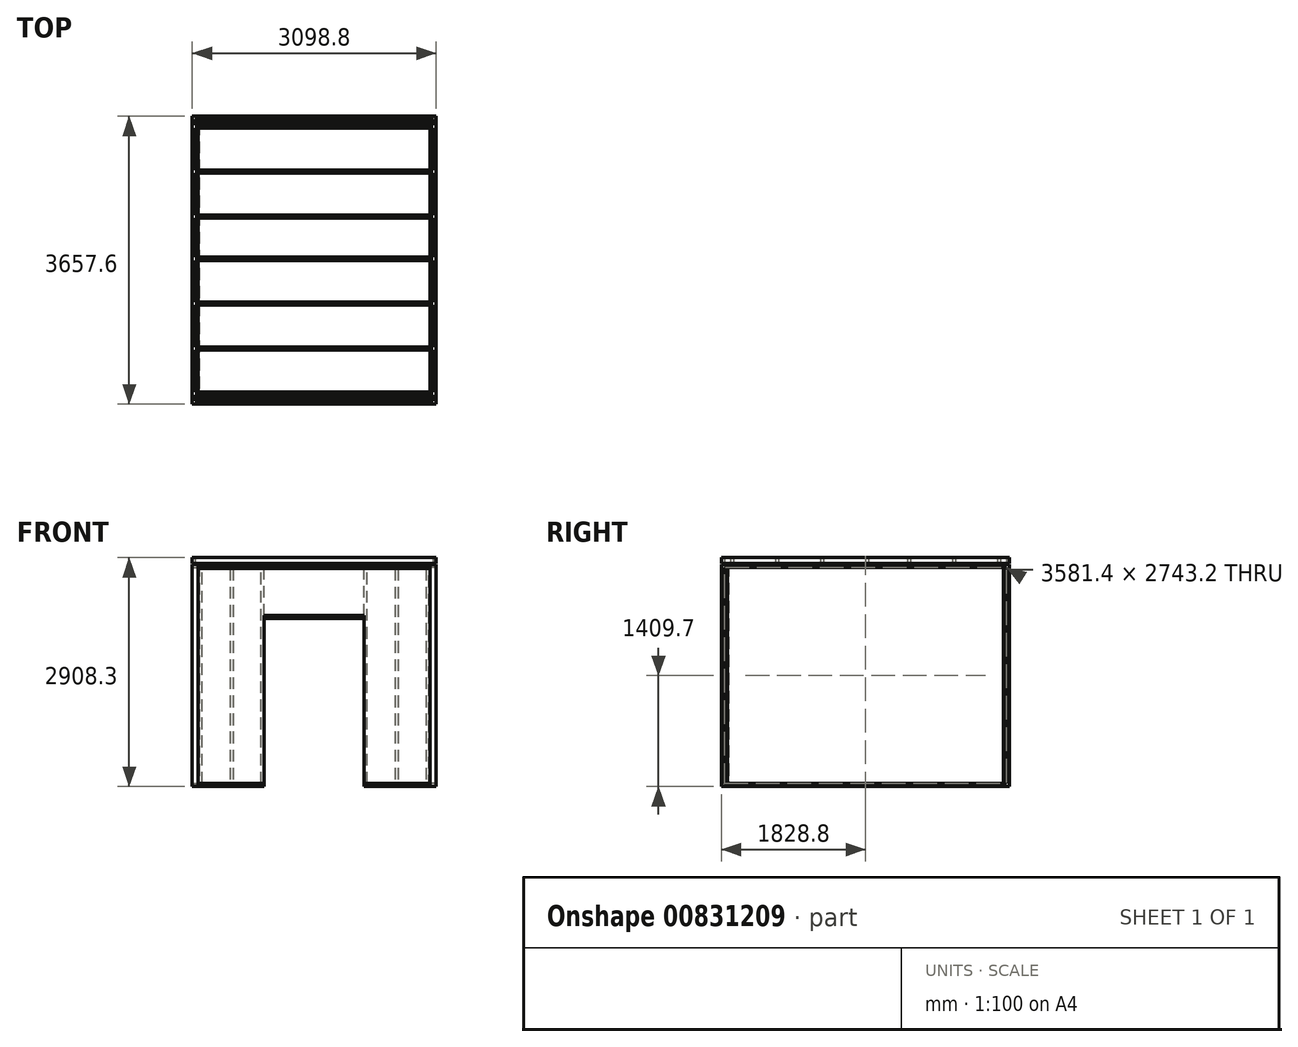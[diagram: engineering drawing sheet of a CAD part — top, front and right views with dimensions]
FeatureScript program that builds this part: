
annotation { "Feature Type Name" : "Feature", "Feature Type Description" : "" }
export const myFeature = defineFeature(function(context is Context, id is Id, definition is map)
    precondition{}
    {
        {
            var Q0;
            Q0=qCreatedBy(makeId("Top.planeOp"),FACE);
            var sketch = newSketch(context, id + "F0", { "sketchPlane" : qUnion([Q0])});
            skLineSegment(sketch, "E0.bottom", {"start": v(-980.79, 2857.66) * mm, "end": v(155.93, 2857.66) * mm});
            skLineSegment(sketch, "E0.top", {"start": v(-980.79, -622.14) * mm, "end": v(1105.1, -622.14) * mm});
            skLineSegment(sketch, "E0.left", {"start": v(-980.79, 2857.66) * mm, "end": v(-980.79, -622.14) * mm});
            skLineSegment(sketch, "E0.right", {"start": v(1940.21, 2857.66) * mm, "end": v(1940.21, -622.14) * mm});
            skLineSegment(sketch, "E1.bottom", {"start": v(-993.49, 2870.36) * mm, "end": v(155.93, 2870.36) * mm});
            skLineSegment(sketch, "E1.top", {"start": v(-993.49, -634.84) * mm, "end": v(913.5, -634.84) * mm});
            skLineSegment(sketch, "E1.left", {"start": v(-993.49, 2870.36) * mm, "end": v(-993.49, -634.84) * mm});
            skLineSegment(sketch, "E1.right", {"start": v(1952.91, 2870.36) * mm, "end": v(1952.91, -634.84) * mm});
            skLineSegment(sketch, "E2.trimOffspring", {"start": v(153.53, 2870.36) * mm, "end": v(1952.91, 2870.36) * mm});
            skLineSegment(sketch, "E3.trimOffspring", {"start": v(149.76, 2857.66) * mm, "end": v(1940.21, 2857.66) * mm});
            skLineSegment(sketch, "E4.trimOffspring", {"start": v(1102.01, -622.14) * mm, "end": v(1940.21, -622.14) * mm});
            skLineSegment(sketch, "E5.trimOffspring", {"start": v(882.21, -634.84) * mm, "end": v(1952.91, -634.84) * mm});
            skSolve(sketch);
        }
        {
            var Q0;
            Q0=makeQuery(id+"F0.imprint","IMPRINT",FACE,{"disambiguationData":[TD([[makeQuery(id+"F0.imprint","IMPRINT",EDGE,{"derivedFrom":sQuery(id+"F0.wireOp",EDGE,"E0.bottom")}),1.0]])]});
            var Q1;
            Q1=makeQuery(id+"F0.imprint","IMPRINT",FACE,{"disambiguationData":[TD([[makeQuery(id+"F0.imprint","IMPRINT",EDGE,{"derivedFrom":sQuery(id+"F0.wireOp",EDGE,"E0.right")}),1.0]])]});
            extrude(context, id + "F1", {"entities" : qUnion([Q0, Q1]), "depth" : 2133.6 * mm + 685.8 * mm, "offsetDistance" : 25.4 * mm});
        }
        {
            var Q0;
            Q0=makeQuery(id+"F1.opExtrude","CAP_FACE",FACE,{"disambiguationData":[OSD([sQuery(id+"F0.wireOp",EDGE,"E0.bottom"),sQuery(id+"F0.wireOp",EDGE,"E0.top"),sQuery(id+"F0.wireOp",EDGE,"E0.left"),sQuery(id+"F0.wireOp",EDGE,"E1.bottom"),sQuery(id+"F0.wireOp",EDGE,"E1.top"),sQuery(id+"F0.wireOp",EDGE,"E1.left"),sQuery(id+"F0.wireOp",EDGE,"ajJvUeQd-ddKz-yDWU-SHTq-AfXzZqwUQA1N.left"),sQuery(id+"F0.wireOp",EDGE,"rDKjrFLu-EuC5-olRp-ZrVZ-GupeaafQM4Xr")])],"isStart":false});
            var sketch = newSketch(context, id + "F2", { "sketchPlane" : qUnion([Q0])});
            skPoint(sketch, "E6.0", {"position": v(1952.91, 2870.36) * mm});
            skPoint(sketch, "E7.0", {"position": v(-993.49, 2870.36) * mm});
            skPoint(sketch, "E8.0", {"position": v(-993.49, -634.84) * mm});
            skLineSegment(sketch, "E9.bottom", {"start": v(-993.49, -634.84) * mm, "end": v(1952.91, -634.84) * mm});
            skLineSegment(sketch, "E9.top", {"start": v(-993.49, 2870.36) * mm, "end": v(1952.91, 2870.36) * mm});
            skLineSegment(sketch, "E9.left", {"start": v(-993.49, -634.84) * mm, "end": v(-993.49, 2870.36) * mm});
            skLineSegment(sketch, "E9.right", {"start": v(1952.91, -634.84) * mm, "end": v(1952.91, 2870.36) * mm});
            skSolve(sketch);
        }
        {
            var Q0;
            Q0 = qSketchRegion(id + "F2", true);
            extrude(context, id + "F3", {"entities" : qUnion([Q0]), "depth" : 12.7 * mm, "offsetDistance" : 25.4 * mm});
        }
        {
            var Q0;
            Q0=makeQuery(id+"F1.opExtrude","SWEPT_FACE",FACE,{"disambiguationData":[OSD([sQuery(id+"F0.wireOp",EDGE,"E1.top"),sQuery(id+"F0.wireOp",EDGE,"E5.trimOffspring")])]});
            var sketch = newSketch(context, id + "F4", { "sketchPlane" : qUnion([Q0])});
            skLineSegment(sketch, "E10.bottom", {"start": v(-155.29, 0) * mm, "end": v(1114.71, 0) * mm});
            skLineSegment(sketch, "E10.top", {"start": v(-155.29, 2133.6) * mm, "end": v(1114.71, 2133.6) * mm});
            skLineSegment(sketch, "E10.left", {"start": v(-155.29, 0) * mm, "end": v(-155.29, 2133.6) * mm});
            skLineSegment(sketch, "E10.right", {"start": v(1114.71, 0) * mm, "end": v(1114.71, 2133.6) * mm});
            skSolve(sketch);
        }
        {
            var Q0;
            Q0=makeQuery(id+"F4.imprint","IMPRINT",FACE,{"disambiguationData":[TD([[makeQuery(id+"F4.imprint","IMPRINT",EDGE,{"derivedFrom":sQuery(id+"F4.wireOp",EDGE,"E10.bottom")}),1.0]])]});
            extrude(context, id + "F5", {"entities" : qUnion([Q0]), "operationType" : NewBodyOperationType.REMOVE, "endBound" : BoundingType.THROUGH_ALL, "oppositeDirection" : true, "depth" : 25.4 * mm, "offsetDistance" : 25.4 * mm});
        }
        {
            var Q0;
            Q0=makeQuery(id+"F1.opExtrude","SWEPT_FACE",FACE,{"disambiguationData":[OSD([sQuery(id+"F0.wireOp",EDGE,"E1.top"),sQuery(id+"F0.wireOp",EDGE,"E5.trimOffspring")])]});
            var sketch = newSketch(context, id + "F6", { "sketchPlane" : qUnion([Q0])});
            skLineSegment(sketch, "E11.bottom", {"start": v(-980.79, 0) * mm, "end": v(-155.29, 0) * mm});
            skLineSegment(sketch, "E11.top", {"start": v(-980.79, 38.1) * mm, "end": v(-155.29, 38.1) * mm});
            skLineSegment(sketch, "E11.right", {"start": v(-155.29, 0) * mm, "end": v(-155.29, 38.1) * mm});
            skLineSegment(sketch, "E12.bottom", {"start": v(-980.79, 38.1) * mm, "end": v(-942.69, 38.1) * mm});
            skLineSegment(sketch, "E12.top", {"start": v(-980.79, 2768.6) * mm, "end": v(-942.69, 2768.6) * mm});
            skLineSegment(sketch, "E12.left", {"start": v(-980.79, 38.1) * mm, "end": v(-980.79, 2768.6) * mm});
            skLineSegment(sketch, "E12.right", {"start": v(-942.69, 38.1) * mm, "end": v(-942.69, 2768.6) * mm});
            skLineSegment(sketch, "E13.bottom", {"start": v(-980.79, 2768.6) * mm, "end": v(1940.21, 2768.6) * mm});
            skLineSegment(sketch, "E13.top", {"start": v(-980.79, 2806.7) * mm, "end": v(1940.21, 2806.7) * mm});
            skLineSegment(sketch, "E13.left", {"start": v(-980.79, 2768.6) * mm, "end": v(-980.79, 2806.7) * mm});
            skLineSegment(sketch, "E13.right", {"start": v(1940.21, 2768.6) * mm, "end": v(1940.21, 2806.7) * mm});
            skLineSegment(sketch, "E14.bottom", {"start": v(1940.21, 2768.6) * mm, "end": v(1902.11, 2768.6) * mm});
            skLineSegment(sketch, "E14.top", {"start": v(1940.21, 38.1) * mm, "end": v(1902.11, 38.1) * mm});
            skLineSegment(sketch, "E14.left", {"start": v(1940.21, 2768.6) * mm, "end": v(1940.21, 38.1) * mm});
            skLineSegment(sketch, "E14.right", {"start": v(1902.11, 2768.6) * mm, "end": v(1902.11, 38.1) * mm});
            skLineSegment(sketch, "E15.bottom", {"start": v(1940.21, 38.1) * mm, "end": v(1114.71, 38.1) * mm});
            skLineSegment(sketch, "E15.top", {"start": v(1940.21, 0) * mm, "end": v(1114.71, 0) * mm});
            skLineSegment(sketch, "E15.left", {"start": v(1940.21, 38.1) * mm, "end": v(1940.21, 0) * mm});
            skLineSegment(sketch, "E15.right", {"start": v(1114.71, 38.1) * mm, "end": v(1114.71, 0) * mm});
            skLineSegment(sketch, "E16.bottom", {"start": v(1114.71, 38.1) * mm, "end": v(1152.81, 38.1) * mm});
            skLineSegment(sketch, "E16.top", {"start": v(1114.71, 2768.6) * mm, "end": v(1152.81, 2768.6) * mm});
            skLineSegment(sketch, "E16.left", {"start": v(1114.71, 38.1) * mm, "end": v(1114.71, 2768.6) * mm});
            skLineSegment(sketch, "E16.right", {"start": v(1152.81, 38.1) * mm, "end": v(1152.81, 2768.6) * mm});
            skLineSegment(sketch, "E17.bottom", {"start": v(1114.71, 2133.6) * mm, "end": v(-155.29, 2133.6) * mm});
            skLineSegment(sketch, "E17.top", {"start": v(1114.71, 2171.7) * mm, "end": v(-155.29, 2171.7) * mm});
            skLineSegment(sketch, "E17.left", {"start": v(1114.71, 2133.6) * mm, "end": v(1114.71, 2171.7) * mm});
            skLineSegment(sketch, "E17.right", {"start": v(-155.29, 2133.6) * mm, "end": v(-155.29, 2171.7) * mm});
            skLineSegment(sketch, "E18.bottom", {"start": v(-155.29, 38.1) * mm, "end": v(-193.39, 38.1) * mm});
            skLineSegment(sketch, "E18.top", {"start": v(-155.29, 2768.6) * mm, "end": v(-193.39, 2768.6) * mm});
            skLineSegment(sketch, "E18.left", {"start": v(-155.29, 38.1) * mm, "end": v(-155.29, 2768.6) * mm});
            skLineSegment(sketch, "E18.right", {"start": v(-193.39, 38.1) * mm, "end": v(-193.39, 2768.6) * mm});
            skLineSegment(sketch, "E19.bottom", {"start": v(-587.09, 2768.6) * mm, "end": v(-548.99, 2768.6) * mm});
            skLineSegment(sketch, "E19.top", {"start": v(-587.09, 38.1) * mm, "end": v(-548.99, 38.1) * mm});
            skLineSegment(sketch, "E19.left", {"start": v(-587.09, 2768.6) * mm, "end": v(-587.09, 38.1) * mm});
            skLineSegment(sketch, "E19.right", {"start": v(-548.99, 2768.6) * mm, "end": v(-548.99, 38.1) * mm});
            skLineSegment(sketch, "E20.bottom", {"start": v(1508.41, 2768.6) * mm, "end": v(1546.51, 2768.6) * mm});
            skLineSegment(sketch, "E20.top", {"start": v(1508.41, 38.1) * mm, "end": v(1546.51, 38.1) * mm});
            skLineSegment(sketch, "E20.left", {"start": v(1508.41, 2768.6) * mm, "end": v(1508.41, 38.1) * mm});
            skLineSegment(sketch, "E20.right", {"start": v(1546.51, 2768.6) * mm, "end": v(1546.51, 38.1) * mm});
            skLineSegment(sketch, "E21", {"start": v(-980.79, 38.1) * mm, "end": v(-980.79, 0) * mm});
            skSolve(sketch);
        }
        {
            var Q0;
            Q0=makeQuery(id+"F6.imprint","IMPRINT",FACE,{"disambiguationData":[TD([[makeQuery(id+"F6.imprint","IMPRINT",EDGE,{"derivedFrom":sQuery(id+"F6.wireOp",EDGE,"E13.top")}),-1.0]])]});
            var Q1;
            Q1=makeQuery(id+"F6.imprint","IMPRINT",FACE,{"disambiguationData":[TD([[makeQuery(id+"F6.imprint","IMPRINT",EDGE,{"derivedFrom":sQuery(id+"F6.wireOp",EDGE,"E12.bottom")}),1.0]])]});
            var Q2;
            Q2=makeQuery(id+"F6.imprint","IMPRINT",FACE,{"disambiguationData":[TD([[makeQuery(id+"F6.imprint","IMPRINT",EDGE,{"derivedFrom":sQuery(id+"F6.wireOp",EDGE,"E19.bottom")}),-1.0]])]});
            var Q3;
            {var subQ3=sQuery(id+"F6.wireOp",EDGE,"E18.bottom");Q3=makeQuery(id+"F6.imprint","IMPRINT",FACE,{"disambiguationData":[TD([[makeQuery(id+"F6.imprint","IMPRINT",EDGE,{"derivedFrom":subQ3}),-1.0]])]});}
            var Q4;
            {var subQ0=sQuery(id+"F6.wireOp",EDGE,"E17.bottom");Q4=makeQuery(id+"F6.imprint","IMPRINT",FACE,{"disambiguationData":[TD([[makeQuery(id+"F6.imprint","IMPRINT",EDGE,{"derivedFrom":subQ0}),1.0]])]});}
            var Q5;
            {var subQ3=sQuery(id+"F6.wireOp",EDGE,"E16.bottom");Q5=makeQuery(id+"F6.imprint","IMPRINT",FACE,{"disambiguationData":[TD([[makeQuery(id+"F6.imprint","IMPRINT",EDGE,{"derivedFrom":subQ3}),1.0]])]});}
            var Q6;
            Q6=makeQuery(id+"F6.imprint","IMPRINT",FACE,{"disambiguationData":[TD([[makeQuery(id+"F6.imprint","IMPRINT",EDGE,{"derivedFrom":sQuery(id+"F6.wireOp",EDGE,"E20.bottom")}),-1.0]])]});
            var Q7;
            Q7=makeQuery(id+"F6.imprint","IMPRINT",FACE,{"disambiguationData":[TD([[makeQuery(id+"F6.imprint","IMPRINT",EDGE,{"derivedFrom":sQuery(id+"F6.wireOp",EDGE,"E14.bottom")}),1.0]])]});
            var Q8;
            Q8=makeQuery(id+"F6.imprint","IMPRINT",FACE,{"disambiguationData":[TD([[makeQuery(id+"F6.imprint","IMPRINT",EDGE,{"derivedFrom":sQuery(id+"F6.wireOp",EDGE,"E15.top")}),1.0]])]});
            var Q9;
            Q9=makeQuery(id+"F6.imprint","IMPRINT",FACE,{"disambiguationData":[TD([[makeQuery(id+"F6.imprint","IMPRINT",EDGE,{"derivedFrom":sQuery(id+"F6.wireOp",EDGE,"E11.bottom")}),1.0]])]});
            extrude(context, id + "F7", {"entities" : qUnion([Q0, Q1, Q2, Q3, Q4, Q5, Q6, Q7, Q8, Q9]), "operationType" : NewBodyOperationType.ADD, "depth" : 76.2 * mm, "offsetDistance" : 25.4 * mm});
        }
        {
            var Q0;
            Q0=makeQuery(id+"F1.opExtrude","SWEPT_FACE",FACE,{"disambiguationData":[OSD([sQuery(id+"F0.wireOp",EDGE,"E1.bottom"),sQuery(id+"F0.wireOp",EDGE,"E2.trimOffspring")])]});
            var sketch = newSketch(context, id + "F8", { "sketchPlane" : qUnion([Q0])});
            skLineSegment(sketch, "E22.0", {"start": v(587.09, 2768.6) * mm, "end": v(587.09, 38.1) * mm});
            skLineSegment(sketch, "E22.1", {"start": v(-1114.71, 0) * mm, "end": v(-1114.71, 2133.6) * mm});
            skLineSegment(sketch, "E22.2", {"start": v(548.99, 2768.6) * mm, "end": v(548.99, 38.1) * mm});
            skLineSegment(sketch, "E22.3", {"start": v(-1508.41, 2768.6) * mm, "end": v(-1508.41, 38.1) * mm});
            skLineSegment(sketch, "E22.4", {"start": v(155.29, 0) * mm, "end": v(155.29, 2133.6) * mm});
            skLineSegment(sketch, "E22.5", {"start": v(980.79, 2806.7) * mm, "end": v(-1940.21, 2806.7) * mm});
            skLineSegment(sketch, "E22.6", {"start": v(-1152.81, 38.1) * mm, "end": v(-1152.81, 2768.6) * mm});
            skLineSegment(sketch, "E22.7", {"start": v(-1546.51, 2768.6) * mm, "end": v(-1546.51, 38.1) * mm});
            skLineSegment(sketch, "E22.8", {"start": v(980.79, 0) * mm, "end": v(980.79, 2806.7) * mm});
            skLineSegment(sketch, "E22.9", {"start": v(-1940.21, 0) * mm, "end": v(-1940.21, 2806.7) * mm});
            skLineSegment(sketch, "E22.10", {"start": v(155.29, 2133.6) * mm, "end": v(-1114.71, 2133.6) * mm});
            skLineSegment(sketch, "E22.11", {"start": v(942.69, 38.1) * mm, "end": v(942.69, 2768.6) * mm});
            skLineSegment(sketch, "E22.12", {"start": v(-1902.11, 2768.6) * mm, "end": v(-1902.11, 38.1) * mm});
            skLineSegment(sketch, "E23.0", {"start": v(942.69, 2768.6) * mm, "end": v(587.09, 2768.6) * mm});
            skLineSegment(sketch, "E24.0", {"start": v(548.99, 2768.6) * mm, "end": v(193.39, 2768.6) * mm});
            skLineSegment(sketch, "E25.0", {"start": v(155.29, 2768.6) * mm, "end": v(-1114.71, 2768.6) * mm});
            skLineSegment(sketch, "E26.0.0", {"start": v(155.29, 2171.7) * mm, "end": v(155.29, 2768.6) * mm});
            skLineSegment(sketch, "E26.0.2", {"start": v(155.29, 2768.6) * mm, "end": v(155.29, 2171.7) * mm});
            skLineSegment(sketch, "E27.0.0", {"start": v(-1114.71, 0) * mm, "end": v(-1940.21, 0) * mm});
            skLineSegment(sketch, "E27.0.2", {"start": v(-1940.21, 2806.7) * mm, "end": v(980.79, 2806.7) * mm});
            skLineSegment(sketch, "E27.0.3", {"start": v(980.79, 2806.7) * mm, "end": v(980.79, 0) * mm});
            skLineSegment(sketch, "E27.0.4", {"start": v(980.79, 0) * mm, "end": v(155.29, 0) * mm});
            skLineSegment(sketch, "E27.0.7", {"start": v(-1114.71, 2133.6) * mm, "end": v(-1114.71, 0) * mm});
            skLineSegment(sketch, "E28.0", {"start": v(-1114.71, 2171.7) * mm, "end": v(-1114.71, 2768.6) * mm});
            skLineSegment(sketch, "E29.0", {"start": v(-1114.71, 2171.7) * mm, "end": v(155.29, 2171.7) * mm});
            skLineSegment(sketch, "E30.0.0", {"start": v(193.39, 2768.6) * mm, "end": v(548.99, 2768.6) * mm});
            skLineSegment(sketch, "E30.0.2", {"start": v(548.99, 38.1) * mm, "end": v(193.39, 38.1) * mm});
            skLineSegment(sketch, "E30.0.3", {"start": v(193.39, 38.1) * mm, "end": v(193.39, 2768.6) * mm});
            skLineSegment(sketch, "E31.0", {"start": v(-1152.81, 2768.6) * mm, "end": v(-1508.41, 2768.6) * mm});
            skLineSegment(sketch, "E32.0", {"start": v(-1546.51, 2768.6) * mm, "end": v(-1902.11, 2768.6) * mm});
            skLineSegment(sketch, "E33.0", {"start": v(-1902.11, 38.1) * mm, "end": v(-1546.51, 38.1) * mm});
            skLineSegment(sketch, "E34.0", {"start": v(-1508.41, 38.1) * mm, "end": v(-1152.81, 38.1) * mm});
            skLineSegment(sketch, "E35.0", {"start": v(942.69, 38.1) * mm, "end": v(587.09, 38.1) * mm});
            skSolve(sketch);
        }
        {
            var Q0;
            Q0 = qSketchRegion(id + "F8", true);
            extrude(context, id + "F9", {"entities" : qUnion([Q0]), "operationType" : NewBodyOperationType.ADD, "depth" : 76.2 * mm, "offsetDistance" : 25.4 * mm});
        }
        {
            var Q0;
            Q0=makeQuery(id+"F1.opExtrude","SWEPT_FACE",FACE,{"disambiguationData":[OSD([sQuery(id+"F0.wireOp",EDGE,"E1.right")])]});
            var sketch = newSketch(context, id + "F10", { "sketchPlane" : qUnion([Q0])});
            skLineSegment(sketch, "E36.bottom", {"start": v(-711.04, 2819.4) * mm, "end": v(2946.56, 2819.4) * mm});
            skLineSegment(sketch, "E36.top", {"start": v(-711.04, 2781.3) * mm, "end": v(2946.56, 2781.3) * mm});
            skLineSegment(sketch, "E36.left", {"start": v(-711.04, 2819.4) * mm, "end": v(-711.04, 2781.3) * mm});
            skLineSegment(sketch, "E36.right", {"start": v(2946.56, 2819.4) * mm, "end": v(2946.56, 2781.3) * mm});
            skPoint(sketch, "E37.0", {"position": v(2946.56, 2806.7) * mm});
            skPoint(sketch, "E38.0", {"position": v(-711.04, 2806.7) * mm});
            skPoint(sketch, "E39.0", {"position": v(-711.04, 0) * mm});
            skPoint(sketch, "E40.0", {"position": v(2946.56, 0) * mm});
            skLineSegment(sketch, "E41.bottom", {"start": v(2946.56, 0) * mm, "end": v(-711.04, 0) * mm});
            skLineSegment(sketch, "E41.top", {"start": v(2946.56, 38.1) * mm, "end": v(-711.04, 38.1) * mm});
            skLineSegment(sketch, "E41.left", {"start": v(2946.56, 0) * mm, "end": v(2946.56, 38.1) * mm});
            skLineSegment(sketch, "E41.right", {"start": v(-711.04, 0) * mm, "end": v(-711.04, 38.1) * mm});
            skLineSegment(sketch, "E42.bottom", {"start": v(2946.56, 2781.3) * mm, "end": v(2908.46, 2781.3) * mm});
            skLineSegment(sketch, "E42.top", {"start": v(2946.56, 38.1) * mm, "end": v(2908.46, 38.1) * mm});
            skLineSegment(sketch, "E42.left", {"start": v(2946.56, 2781.3) * mm, "end": v(2946.56, 38.1) * mm});
            skLineSegment(sketch, "E42.right", {"start": v(2908.46, 2781.3) * mm, "end": v(2908.46, 38.1) * mm});
            skLineSegment(sketch, "E43.bottom", {"start": v(-711.04, 38.1) * mm, "end": v(-672.94, 38.1) * mm});
            skLineSegment(sketch, "E43.top", {"start": v(-711.04, 2781.3) * mm, "end": v(-672.94, 2781.3) * mm});
            skLineSegment(sketch, "E43.left", {"start": v(-711.04, 38.1) * mm, "end": v(-711.04, 2781.3) * mm});
            skLineSegment(sketch, "E43.right", {"start": v(-672.94, 38.1) * mm, "end": v(-672.94, 2781.3) * mm});
            skLineSegment(sketch, "E44.bottom", {"start": v(-596.74, 2781.3) * mm, "end": v(-558.64, 2781.3) * mm});
            skLineSegment(sketch, "E44.top", {"start": v(-596.74, 38.1) * mm, "end": v(-558.64, 38.1) * mm});
            skLineSegment(sketch, "E44.left", {"start": v(-596.74, 2781.3) * mm, "end": v(-596.74, 38.1) * mm});
            skLineSegment(sketch, "E44.right", {"start": v(-558.64, 2781.3) * mm, "end": v(-558.64, 38.1) * mm});
            skLineSegment(sketch, "E45.bottom", {"start": v(2832.26, 2781.3) * mm, "end": v(2794.16, 2781.3) * mm});
            skLineSegment(sketch, "E45.top", {"start": v(2832.26, 38.1) * mm, "end": v(2794.16, 38.1) * mm});
            skLineSegment(sketch, "E45.left", {"start": v(2832.26, 2781.3) * mm, "end": v(2832.26, 38.1) * mm});
            skLineSegment(sketch, "E45.right", {"start": v(2794.16, 2781.3) * mm, "end": v(2794.16, 38.1) * mm});
            skLineSegment(sketch, "E46.bottom", {"start": v(-25.24, 38.1) * mm, "end": v(12.86, 38.1) * mm});
            skLineSegment(sketch, "E46.top", {"start": v(-25.24, 2781.3) * mm, "end": v(12.86, 2781.3) * mm});
            skLineSegment(sketch, "E46.left", {"start": v(-25.24, 38.1) * mm, "end": v(-25.24, 2781.3) * mm});
            skLineSegment(sketch, "E46.right", {"start": v(12.86, 38.1) * mm, "end": v(12.86, 2781.3) * mm});
            skLineSegment(sketch, "E47.bottom", {"start": v(546.26, 2781.3) * mm, "end": v(584.36, 2781.3) * mm});
            skLineSegment(sketch, "E47.top", {"start": v(546.26, 38.1) * mm, "end": v(584.36, 38.1) * mm});
            skLineSegment(sketch, "E47.left", {"start": v(546.26, 2781.3) * mm, "end": v(546.26, 38.1) * mm});
            skLineSegment(sketch, "E47.right", {"start": v(584.36, 2781.3) * mm, "end": v(584.36, 38.1) * mm});
            skLineSegment(sketch, "E48.bottom", {"start": v(1079.66, 2781.3) * mm, "end": v(1117.76, 2781.3) * mm});
            skLineSegment(sketch, "E48.top", {"start": v(1079.66, 38.1) * mm, "end": v(1117.76, 38.1) * mm});
            skLineSegment(sketch, "E48.left", {"start": v(1079.66, 2781.3) * mm, "end": v(1079.66, 38.1) * mm});
            skLineSegment(sketch, "E48.right", {"start": v(1117.76, 2781.3) * mm, "end": v(1117.76, 38.1) * mm});
            skLineSegment(sketch, "E49.bottom", {"start": v(1651.16, 2781.3) * mm, "end": v(1689.26, 2781.3) * mm});
            skLineSegment(sketch, "E49.top", {"start": v(1651.16, 38.1) * mm, "end": v(1689.26, 38.1) * mm});
            skLineSegment(sketch, "E49.left", {"start": v(1651.16, 2781.3) * mm, "end": v(1651.16, 38.1) * mm});
            skLineSegment(sketch, "E49.right", {"start": v(1689.26, 2781.3) * mm, "end": v(1689.26, 38.1) * mm});
            skLineSegment(sketch, "E50.bottom", {"start": v(2222.66, 2781.3) * mm, "end": v(2260.76, 2781.3) * mm});
            skLineSegment(sketch, "E50.top", {"start": v(2222.66, 38.1) * mm, "end": v(2260.76, 38.1) * mm});
            skLineSegment(sketch, "E50.left", {"start": v(2222.66, 2781.3) * mm, "end": v(2222.66, 38.1) * mm});
            skLineSegment(sketch, "E50.right", {"start": v(2260.76, 2781.3) * mm, "end": v(2260.76, 38.1) * mm});
            skSolve(sketch);
        }
        {
            var Q0;
            Q0 = qSketchRegion(id + "F10", true);
            var Q1;
            Q1=makeQuery(id+"F10.imprint","IMPRINT",FACE,{"disambiguationData":[TD([[makeQuery(id+"F10.imprint","IMPRINT",EDGE,{"derivedFrom":sQuery(id+"F10.wireOp",EDGE,"E44.bottom")}),-1.0]])]});
            var Q2;
            Q2=makeQuery(id+"F10.imprint","IMPRINT",FACE,{"disambiguationData":[TD([[makeQuery(id+"F10.imprint","IMPRINT",EDGE,{"derivedFrom":sQuery(id+"F10.wireOp",EDGE,"E46.bottom")}),1.0]])]});
            var Q3;
            Q3=makeQuery(id+"F10.imprint","IMPRINT",FACE,{"disambiguationData":[TD([[makeQuery(id+"F10.imprint","IMPRINT",EDGE,{"derivedFrom":sQuery(id+"F10.wireOp",EDGE,"E47.bottom")}),-1.0]])]});
            var Q4;
            Q4=makeQuery(id+"F10.imprint","IMPRINT",FACE,{"disambiguationData":[TD([[makeQuery(id+"F10.imprint","IMPRINT",EDGE,{"derivedFrom":sQuery(id+"F10.wireOp",EDGE,"E48.bottom")}),-1.0]])]});
            var Q5;
            Q5=makeQuery(id+"F10.imprint","IMPRINT",FACE,{"disambiguationData":[TD([[makeQuery(id+"F10.imprint","IMPRINT",EDGE,{"derivedFrom":sQuery(id+"F10.wireOp",EDGE,"E49.bottom")}),-1.0]])]});
            var Q6;
            Q6=makeQuery(id+"F10.imprint","IMPRINT",FACE,{"disambiguationData":[TD([[makeQuery(id+"F10.imprint","IMPRINT",EDGE,{"derivedFrom":sQuery(id+"F10.wireOp",EDGE,"E50.bottom")}),-1.0]])]});
            var Q7;
            Q7=makeQuery(id+"F10.imprint","IMPRINT",FACE,{"disambiguationData":[TD([[makeQuery(id+"F10.imprint","IMPRINT",EDGE,{"derivedFrom":sQuery(id+"F10.wireOp",EDGE,"E45.bottom")}),1.0]])]});
            extrude(context, id + "F11", {"entities" : qUnion([Q0, Q1, Q2, Q3, Q4, Q5, Q6, Q7]), "operationType" : NewBodyOperationType.ADD, "depth" : 76.2 * mm, "offsetDistance" : 25.4 * mm});
        }
        {
            var Q0;
            Q0=makeQuery(id+"F1.opExtrude","SWEPT_FACE",FACE,{"disambiguationData":[OSD([sQuery(id+"F0.wireOp",EDGE,"E1.left")])]});
            var sketch = newSketch(context, id + "F12", { "sketchPlane" : qUnion([Q0])});
            skLineSegment(sketch, "E51.bottom", {"start": v(-2946.56, 2819.4) * mm, "end": v(711.04, 2819.4) * mm});
            skLineSegment(sketch, "E51.top", {"start": v(-2946.56, 2781.3) * mm, "end": v(711.04, 2781.3) * mm});
            skLineSegment(sketch, "E51.left", {"start": v(-2946.56, 2819.4) * mm, "end": v(-2946.56, 2781.3) * mm});
            skLineSegment(sketch, "E51.right", {"start": v(711.04, 2819.4) * mm, "end": v(711.04, 2781.3) * mm});
            skPoint(sketch, "E52.0", {"position": v(711.04, 2806.7) * mm});
            skPoint(sketch, "E53.0", {"position": v(-2946.56, 0) * mm});
            skPoint(sketch, "E54.0", {"position": v(711.04, 0) * mm});
            skLineSegment(sketch, "E55.bottom", {"start": v(711.04, 0) * mm, "end": v(-2946.56, 0) * mm});
            skLineSegment(sketch, "E55.top", {"start": v(711.04, 38.1) * mm, "end": v(-2946.56, 38.1) * mm});
            skLineSegment(sketch, "E55.left", {"start": v(711.04, 0) * mm, "end": v(711.04, 38.1) * mm});
            skLineSegment(sketch, "E55.right", {"start": v(-2946.56, 0) * mm, "end": v(-2946.56, 38.1) * mm});
            skLineSegment(sketch, "E56.bottom", {"start": v(711.04, 2781.3) * mm, "end": v(672.94, 2781.3) * mm});
            skLineSegment(sketch, "E56.top", {"start": v(711.04, 38.1) * mm, "end": v(672.94, 38.1) * mm});
            skLineSegment(sketch, "E56.left", {"start": v(711.04, 2781.3) * mm, "end": v(711.04, 38.1) * mm});
            skLineSegment(sketch, "E56.right", {"start": v(672.94, 2781.3) * mm, "end": v(672.94, 38.1) * mm});
            skLineSegment(sketch, "E57.bottom", {"start": v(-2946.56, 38.1) * mm, "end": v(-2908.46, 38.1) * mm});
            skLineSegment(sketch, "E57.top", {"start": v(-2946.56, 2781.3) * mm, "end": v(-2908.46, 2781.3) * mm});
            skLineSegment(sketch, "E57.left", {"start": v(-2946.56, 38.1) * mm, "end": v(-2946.56, 2781.3) * mm});
            skLineSegment(sketch, "E57.right", {"start": v(-2908.46, 38.1) * mm, "end": v(-2908.46, 2781.3) * mm});
            skLineSegment(sketch, "E58.bottom", {"start": v(-2832.26, 2781.3) * mm, "end": v(-2794.16, 2781.3) * mm});
            skLineSegment(sketch, "E58.top", {"start": v(-2832.26, 38.1) * mm, "end": v(-2794.16, 38.1) * mm});
            skLineSegment(sketch, "E58.left", {"start": v(-2832.26, 2781.3) * mm, "end": v(-2832.26, 38.1) * mm});
            skLineSegment(sketch, "E58.right", {"start": v(-2794.16, 2781.3) * mm, "end": v(-2794.16, 38.1) * mm});
            skLineSegment(sketch, "E59.bottom", {"start": v(596.74, 2781.3) * mm, "end": v(558.64, 2781.3) * mm});
            skLineSegment(sketch, "E59.top", {"start": v(596.74, 38.1) * mm, "end": v(558.64, 38.1) * mm});
            skLineSegment(sketch, "E59.left", {"start": v(596.74, 2781.3) * mm, "end": v(596.74, 38.1) * mm});
            skLineSegment(sketch, "E59.right", {"start": v(558.64, 2781.3) * mm, "end": v(558.64, 38.1) * mm});
            skLineSegment(sketch, "E60.bottom", {"start": v(-2260.76, 38.1) * mm, "end": v(-2222.66, 38.1) * mm});
            skLineSegment(sketch, "E60.top", {"start": v(-2260.76, 2781.3) * mm, "end": v(-2222.66, 2781.3) * mm});
            skLineSegment(sketch, "E60.left", {"start": v(-2260.76, 38.1) * mm, "end": v(-2260.76, 2781.3) * mm});
            skLineSegment(sketch, "E60.right", {"start": v(-2222.66, 38.1) * mm, "end": v(-2222.66, 2781.3) * mm});
            skLineSegment(sketch, "E61.bottom", {"start": v(-1689.26, 2781.3) * mm, "end": v(-1651.16, 2781.3) * mm});
            skLineSegment(sketch, "E61.top", {"start": v(-1689.26, 38.1) * mm, "end": v(-1651.16, 38.1) * mm});
            skLineSegment(sketch, "E61.left", {"start": v(-1689.26, 2781.3) * mm, "end": v(-1689.26, 38.1) * mm});
            skLineSegment(sketch, "E61.right", {"start": v(-1651.16, 2781.3) * mm, "end": v(-1651.16, 38.1) * mm});
            skLineSegment(sketch, "E62.bottom", {"start": v(-1155.86, 2781.3) * mm, "end": v(-1117.76, 2781.3) * mm});
            skLineSegment(sketch, "E62.top", {"start": v(-1155.86, 38.1) * mm, "end": v(-1117.76, 38.1) * mm});
            skLineSegment(sketch, "E62.left", {"start": v(-1155.86, 2781.3) * mm, "end": v(-1155.86, 38.1) * mm});
            skLineSegment(sketch, "E62.right", {"start": v(-1117.76, 2781.3) * mm, "end": v(-1117.76, 38.1) * mm});
            skLineSegment(sketch, "E63.bottom", {"start": v(-584.36, 2781.3) * mm, "end": v(-546.26, 2781.3) * mm});
            skLineSegment(sketch, "E63.top", {"start": v(-584.36, 38.1) * mm, "end": v(-546.26, 38.1) * mm});
            skLineSegment(sketch, "E63.left", {"start": v(-584.36, 2781.3) * mm, "end": v(-584.36, 38.1) * mm});
            skLineSegment(sketch, "E63.right", {"start": v(-546.26, 2781.3) * mm, "end": v(-546.26, 38.1) * mm});
            skLineSegment(sketch, "E64.bottom", {"start": v(-12.86, 2781.3) * mm, "end": v(25.24, 2781.3) * mm});
            skLineSegment(sketch, "E64.top", {"start": v(-12.86, 38.1) * mm, "end": v(25.24, 38.1) * mm});
            skLineSegment(sketch, "E64.left", {"start": v(-12.86, 2781.3) * mm, "end": v(-12.86, 38.1) * mm});
            skLineSegment(sketch, "E64.right", {"start": v(25.24, 2781.3) * mm, "end": v(25.24, 38.1) * mm});
            skPoint(sketch, "E65.0", {"position": v(-2946.56, 2819.4) * mm});
            skSolve(sketch);
        }
        {
            var Q0;
            Q0 = qSketchRegion(id + "F12", true);
            var Q1;
            Q1=makeQuery(id+"F12.imprint","IMPRINT",FACE,{"disambiguationData":[TD([[makeQuery(id+"F12.imprint","IMPRINT",EDGE,{"derivedFrom":sQuery(id+"F12.wireOp",EDGE,"E58.bottom")}),-1.0]])]});
            var Q2;
            Q2=makeQuery(id+"F12.imprint","IMPRINT",FACE,{"disambiguationData":[TD([[makeQuery(id+"F12.imprint","IMPRINT",EDGE,{"derivedFrom":sQuery(id+"F12.wireOp",EDGE,"E60.bottom")}),1.0]])]});
            var Q3;
            Q3=makeQuery(id+"F12.imprint","IMPRINT",FACE,{"disambiguationData":[TD([[makeQuery(id+"F12.imprint","IMPRINT",EDGE,{"derivedFrom":sQuery(id+"F12.wireOp",EDGE,"E61.bottom")}),-1.0]])]});
            var Q4;
            Q4=makeQuery(id+"F12.imprint","IMPRINT",FACE,{"disambiguationData":[TD([[makeQuery(id+"F12.imprint","IMPRINT",EDGE,{"derivedFrom":sQuery(id+"F12.wireOp",EDGE,"E62.bottom")}),-1.0]])]});
            var Q5;
            Q5=makeQuery(id+"F12.imprint","IMPRINT",FACE,{"disambiguationData":[TD([[makeQuery(id+"F12.imprint","IMPRINT",EDGE,{"derivedFrom":sQuery(id+"F12.wireOp",EDGE,"E63.bottom")}),-1.0]])]});
            var Q6;
            Q6=makeQuery(id+"F12.imprint","IMPRINT",FACE,{"disambiguationData":[TD([[makeQuery(id+"F12.imprint","IMPRINT",EDGE,{"derivedFrom":sQuery(id+"F12.wireOp",EDGE,"E64.bottom")}),-1.0]])]});
            var Q7;
            Q7=makeQuery(id+"F12.imprint","IMPRINT",FACE,{"disambiguationData":[TD([[makeQuery(id+"F12.imprint","IMPRINT",EDGE,{"derivedFrom":sQuery(id+"F12.wireOp",EDGE,"E59.bottom")}),1.0]])]});
            extrude(context, id + "F13", {"entities" : qUnion([Q0, Q1, Q2, Q3, Q4, Q5, Q6, Q7]), "operationType" : NewBodyOperationType.ADD, "depth" : 76.2 * mm, "offsetDistance" : 25.4 * mm});
        }
        {
            var Q0;
            Q0=makeQuery(id+"F3.opExtrude","CAP_FACE",FACE,{"disambiguationData":[OSD([sQuery(id+"F2.wireOp",EDGE,"E9.bottom"),sQuery(id+"F2.wireOp",EDGE,"E9.top"),sQuery(id+"F2.wireOp",EDGE,"E9.left"),sQuery(id+"F2.wireOp",EDGE,"E9.right")])],"isStart":false});
            var sketch = newSketch(context, id + "F14", { "sketchPlane" : qUnion([Q0])});
            skPoint(sketch, "E66.0", {"position": v(-1069.69, 2946.56) * mm});
            skPoint(sketch, "E67.0", {"position": v(2029.11, -711.04) * mm});
            skLineSegment(sketch, "E68.bottom", {"start": v(2029.11, -711.04) * mm, "end": v(-1069.69, -711.04) * mm});
            skLineSegment(sketch, "E68.top", {"start": v(2029.11, 2946.56) * mm, "end": v(-1069.69, 2946.56) * mm});
            skLineSegment(sketch, "E68.left", {"start": v(2029.11, -711.04) * mm, "end": v(2029.11, 2946.56) * mm});
            skLineSegment(sketch, "E68.right", {"start": v(-1069.69, -711.04) * mm, "end": v(-1069.69, 2946.56) * mm});
            skLineSegment(sketch, "E69.bottom", {"start": v(-1031.59, 2906.43) * mm, "end": v(1991.01, 2906.43) * mm});
            skLineSegment(sketch, "E69.top", {"start": v(-1031.59, -672.94) * mm, "end": v(1991.01, -672.94) * mm});
            skLineSegment(sketch, "E69.left", {"start": v(-1031.59, 2906.43) * mm, "end": v(-1031.59, 2832.26) * mm});
            skLineSegment(sketch, "E69.right", {"start": v(1991.01, 2906.43) * mm, "end": v(1991.01, 2832.26) * mm});
            skPoint(sketch, "E70.0", {"position": v(-1069.69, 2260.76) * mm});
            skPoint(sketch, "E71.0", {"position": v(-1069.69, 1689.26) * mm});
            skPoint(sketch, "E72.0", {"position": v(-1069.69, 1155.86) * mm});
            skPoint(sketch, "E73.0", {"position": v(-1069.69, 584.36) * mm});
            skPoint(sketch, "E74.0", {"position": v(-1069.69, 546.26) * mm});
            skPoint(sketch, "E75.0", {"position": v(-1069.69, 1117.76) * mm});
            skPoint(sketch, "E76.0", {"position": v(-1069.69, 1651.16) * mm});
            skPoint(sketch, "E77.0", {"position": v(-1069.69, 2222.66) * mm});
            skPoint(sketch, "E78.0", {"position": v(-1069.69, 2832.26) * mm});
            skPoint(sketch, "E79.0", {"position": v(-1069.69, 2794.16) * mm});
            skPoint(sketch, "E80.0", {"position": v(-1069.69, 12.86) * mm});
            skPoint(sketch, "E81.0", {"position": v(-1069.69, -25.24) * mm});
            skPoint(sketch, "E82.0", {"position": v(-1069.69, -558.64) * mm});
            skPoint(sketch, "E83.0", {"position": v(-1069.69, -596.74) * mm});
            skLineSegment(sketch, "E84.bottom", {"start": v(-1031.59, 2832.26) * mm, "end": v(1991.01, 2832.26) * mm});
            skLineSegment(sketch, "E84.top", {"start": v(-1031.59, 2794.16) * mm, "end": v(1991.01, 2794.16) * mm});
            skLineSegment(sketch, "E84.left", {"start": v(-1069.69, 2832.26) * mm, "end": v(-1069.69, 2794.16) * mm});
            skLineSegment(sketch, "E84.right", {"start": v(2029.11, 2832.26) * mm, "end": v(2029.11, 2794.16) * mm});
            skLineSegment(sketch, "E85.bottom", {"start": v(-1031.59, 2260.76) * mm, "end": v(1991.01, 2260.76) * mm});
            skLineSegment(sketch, "E85.top", {"start": v(-1031.59, 2222.66) * mm, "end": v(1991.01, 2222.66) * mm});
            skLineSegment(sketch, "E85.left", {"start": v(-1069.69, 2260.76) * mm, "end": v(-1069.69, 2222.66) * mm});
            skLineSegment(sketch, "E85.right", {"start": v(2029.11, 2260.76) * mm, "end": v(2029.11, 2222.66) * mm});
            skLineSegment(sketch, "E86.bottom", {"start": v(-1031.59, 1689.26) * mm, "end": v(1991.01, 1689.26) * mm});
            skLineSegment(sketch, "E86.top", {"start": v(-1031.59, 1651.16) * mm, "end": v(1991.01, 1651.16) * mm});
            skLineSegment(sketch, "E86.left", {"start": v(-1069.69, 1689.26) * mm, "end": v(-1069.69, 1651.16) * mm});
            skLineSegment(sketch, "E86.right", {"start": v(2029.11, 1689.26) * mm, "end": v(2029.11, 1651.16) * mm});
            skPoint(sketch, "E87.oppositeSnap0", {"position": v(1991.01, 1116.74) * mm});
            skLineSegment(sketch, "E87.bottom", {"start": v(-1031.59, 1155.86) * mm, "end": v(1991.01, 1155.86) * mm});
            skLineSegment(sketch, "E87.top", {"start": v(-1031.59, 1116.74) * mm, "end": v(1991.01, 1116.74) * mm});
            skLineSegment(sketch, "E87.left", {"start": v(-1069.69, 1155.86) * mm, "end": v(-1069.69, 1116.74) * mm});
            skLineSegment(sketch, "E87.right", {"start": v(2029.11, 1155.86) * mm, "end": v(2029.11, 1116.74) * mm});
            skLineSegment(sketch, "E88.bottom", {"start": v(-1031.59, -558.64) * mm, "end": v(1991.01, -558.64) * mm});
            skLineSegment(sketch, "E88.top", {"start": v(-1031.59, -596.74) * mm, "end": v(1991.01, -596.74) * mm});
            skLineSegment(sketch, "E88.left", {"start": v(-1069.69, -558.64) * mm, "end": v(-1069.69, -596.74) * mm});
            skLineSegment(sketch, "E88.right", {"start": v(2029.11, -558.64) * mm, "end": v(2029.11, -596.74) * mm});
            skLineSegment(sketch, "E89.bottom", {"start": v(-1031.59, -25.24) * mm, "end": v(1991.01, -25.24) * mm});
            skLineSegment(sketch, "E89.top", {"start": v(-1031.59, 12.86) * mm, "end": v(1991.01, 12.86) * mm});
            skLineSegment(sketch, "E89.left", {"start": v(-1069.69, -25.24) * mm, "end": v(-1069.69, 12.86) * mm});
            skLineSegment(sketch, "E89.right", {"start": v(2029.11, -25.24) * mm, "end": v(2029.11, 12.86) * mm});
            skLineSegment(sketch, "E90.bottom", {"start": v(-1031.59, 546.26) * mm, "end": v(1991.01, 546.26) * mm});
            skLineSegment(sketch, "E90.top", {"start": v(-1031.59, 584.36) * mm, "end": v(1991.01, 584.36) * mm});
            skLineSegment(sketch, "E90.left", {"start": v(-1069.69, 546.26) * mm, "end": v(-1069.69, 584.36) * mm});
            skLineSegment(sketch, "E90.right", {"start": v(2029.11, 546.26) * mm, "end": v(2029.11, 584.36) * mm});
            skLineSegment(sketch, "E91.trimOffspring", {"start": v(-1031.59, -596.74) * mm, "end": v(-1031.59, -672.94) * mm});
            skLineSegment(sketch, "E92.trimOffspring", {"start": v(-1031.59, -25.24) * mm, "end": v(-1031.59, -558.64) * mm});
            skLineSegment(sketch, "E93.trimOffspring", {"start": v(-1031.59, 546.26) * mm, "end": v(-1031.59, 12.86) * mm});
            skLineSegment(sketch, "E94.trimOffspring", {"start": v(-1031.59, 1116.74) * mm, "end": v(-1031.59, 584.36) * mm});
            skLineSegment(sketch, "E95.trimOffspring", {"start": v(-1031.59, 1651.16) * mm, "end": v(-1031.59, 1155.86) * mm});
            skLineSegment(sketch, "E96.trimOffspring", {"start": v(-1031.59, 2222.66) * mm, "end": v(-1031.59, 1689.26) * mm});
            skLineSegment(sketch, "E97.trimOffspring", {"start": v(-1031.59, 2794.16) * mm, "end": v(-1031.59, 2260.76) * mm});
            skLineSegment(sketch, "E98.trimOffspring", {"start": v(1991.01, 2794.16) * mm, "end": v(1991.01, 2260.76) * mm});
            skLineSegment(sketch, "E99.trimOffspring", {"start": v(1991.01, 2222.66) * mm, "end": v(1991.01, 1689.26) * mm});
            skLineSegment(sketch, "E100.trimOffspring", {"start": v(1991.01, 1651.16) * mm, "end": v(1991.01, 1155.86) * mm});
            skLineSegment(sketch, "E101.trimOffspring", {"start": v(1991.01, 1116.74) * mm, "end": v(1991.01, 584.36) * mm});
            skLineSegment(sketch, "E102.trimOffspring", {"start": v(1991.01, 546.26) * mm, "end": v(1991.01, 12.86) * mm});
            skLineSegment(sketch, "E103.trimOffspring", {"start": v(1991.01, -25.24) * mm, "end": v(1991.01, -558.64) * mm});
            skLineSegment(sketch, "E104.trimOffspring", {"start": v(1991.01, -596.74) * mm, "end": v(1991.01, -672.94) * mm});
            skSolve(sketch);
        }
        {
            var Q0;
            Q0 = qSketchRegion(id + "F14", true);
            extrude(context, id + "F15", {"entities" : qUnion([Q0]), "operationType" : NewBodyOperationType.ADD, "depth" : 76.2 * mm, "offsetDistance" : 25.4 * mm});
        }
    });
